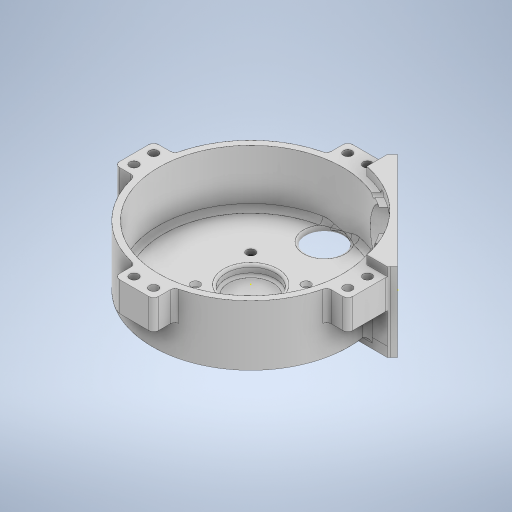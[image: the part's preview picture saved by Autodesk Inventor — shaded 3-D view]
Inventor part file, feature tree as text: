
AUTODESK INVENTOR PART (.ipt)
format: ipt  version: 2023 (Build 270158000, 158)  size: 805,888 bytes
history: native  units: in
note: dims shown in document units (in); Inventor stores cm internally (conversion verified against a paired STEP export)
features: sketch x26, extrude x21, fillet x11, hole x3
ambient origin geometry x8: Origin, YZ Plane, XZ Plane, XY Plane, X Axis, Y Axis, Z Axis, Center Point
bodies: Solid1 (feature_tree)
feature tree (61):
  extrude  "Extrusion1"  Depth=1.375in TaperAngle=0.0deg
  extrude  "Extrusion2"  Depth=1.275in TaperAngle=0.0deg
  extrude  "Extrusion3"  Depth=1.125in TaperAngle=0.0deg
  hole  "Hole1"  [1 undecoded]
  extrude  "Extrusion4"  Depth=0.4in
  extrude  "Extrusion5"  Depth=0.4in
  hole  "Hole2"  [1 undecoded]
  extrude  "Extrusion6"  Depth=0.4in
  sketch  "Sketch10"  dims[d26=0.8in d27=0.4in]
  extrude  "Extrusion7"  Depth=0.4in
  extrude  "Extrusion8"  Depth=0.8in
  extrude  "Extrusion9"  Depth=0.4in
  extrude  "Extrusion18"  Depth=0.75in TaperAngle=0.0deg
  extrude  "Extrusion19"  Depth=0.2in
  extrude  "Extrusion20"  Depth=0.2in
  extrude  "Extrusion21"  Depth=0.4in
  extrude  "Extrusion22"  Depth=0.2in
  extrude  "Extrusion23"  Depth=0.2in
  sketch  "Sketch34"  dims[d125=0.3in d126=0.3in]
  hole  "Hole6"  [1 undecoded]
  extrude  "Extrusion24"  Depth=2.0in TaperAngle=0.0deg
  fillet  "Fillet1"  Radius=2.0in
  fillet  "Fillet2"  Radius=0.3in
  fillet  "Fillet3"  Radius=0.3in
  fillet  "Fillet4"  Radius=0.3in
  fillet  "Fillet5"  Radius=0.3in
  fillet  "Fillet6"  Radius=0.1in
  fillet  "Fillet7"  Radius=0.1in
  fillet  "Fillet8"  Radius=0.175in
  fillet  "Fillet9"  Radius=0.2in
  fillet  "Fillet10"  Radius=1.0875in
  fillet  "Fillet11"  Radius=1.425in
  extrude  "Extrusion25"  Depth=0.5in
  extrude  "Extrusion11"  Depth=0.5in
  extrude  "Extrusion13"  Depth=0.3in
  extrude  "Extrusion14"  Depth=0.3in
  extrude  "Extrusion16"  Depth=1.225in TaperAngle=0.0deg
  sketch  "Sketch1"  dims[d0=4.0in d1=1.375in d2=0.0in]
  sketch  "Sketch2"  dims[d3=3.75in d4=1.275in d5=0.0in]
  sketch  "Sketch3"  dims[d6=1.0in d7=1.125in d8=0.0in]
  sketch  "Sketch4"  dims[d9=1.125in d10=1.125in]
  sketch  "Sketch5"  dims[d11=0.177in d12=0.75in d13=0.332in d14=0.25in d15=0.5635in d16=1.0in d17=0.8108in d18=0.4in]
  sketch  "Sketch6"  dims[d19=0.5in d20=0.4in]
  sketch  "Sketch7"  dims[d21=0.5in d22=0.75in d23=0.0in]
  sketch  "Sketch8"  dims[d24=0.5in d25=0.4in]
  sketch  "Sketch11"  dims[d28=0.5in d29=0.8in]
  sketch  "Sketch12"  dims[d30=0.5in d31=0.4in]
  sketch  "Sketch13"  dims[d32=0.8in d33=0.75in d34=0.0in]
  sketch  "Sketch17"  dims[d35=0.2in d36=0.2in]
  sketch  "Sketch19"  dims[d37=0.4in d38=0.2in]
  sketch  "Sketch20"  dims[d39=0.2in d40=0.4in]
  sketch  "Sketch23"  dims[d41=0.2in d42=0.2in]
  sketch  "Sketch26"  dims[d43=0.2in d44=0.2in]
  sketch  "Sketch27"  dims[d45=0.4in]
  sketch  "Sketch28"  dims[d46=0.177in d47=0.75in d48=0.375in d49=0.25in d50=0.5635in d51=0.75in d52=0.8108in d53=1.5in]
  sketch  "Sketch30"  dims[d54=0.75in d55=0.0in d66=0.15in d67=0.0in d68=2.0in d69=0.3in d70=0.3in d71=0.3in d72=0.3in d73=0.1in d74=0.0in d75=0.1in d76=0.0in d79=0.175in d80=0.0in d84=0.2in d85=0.0in d86=1.0875in d87=0.0in d101=1.425in d102=0.0in]
  sketch  "Sketch32"  dims[d105=0.3in d106=0.0in d122=0.5in]
  sketch  "Sketch33"  dims[d123=0.5in d124=0.5in]
  sketch  "Sketch35"  dims[d127=0.3in d128=0.3in]
  sketch  "Sketch36"  dims[d129=0.175in d130=1.225in d131=0.0in d132=0.0in d133=0.0625in d134=1.125in d135=0.0in d136=0.0in]
  sketch  "Sketch37"  dims[d137=0.15in d138=1.6in d139=0.0in d140=0.375in d141=0.0in d142=0.2in d143=0.0in d144=0.3in d145=0.2in d146=0.0in d147=0.8in d148=1.275in d149=1.275in d150=0.126in d151=0.75in d152=0.248in d153=0.25in d154=90.0deg d155=0.5in d156=0.8108in d157=1.5in d158=0.4in d159=0.0in d160=0.25in d161=0.25in d162=0.25in d163=0.1in d164=0.1in d165=0.1in d166=0.1in d167=0.05in d168=0.05in d169=0.1in d170=0.1in d171=0.175in d172=0.0in d81=0.5in d82=0.0344in]
note: 3 required parameter values undecoded (feature->parameter linkage not recoverable at this tier; creation-order binding heuristic only, values carry confidence <= 0.55)
